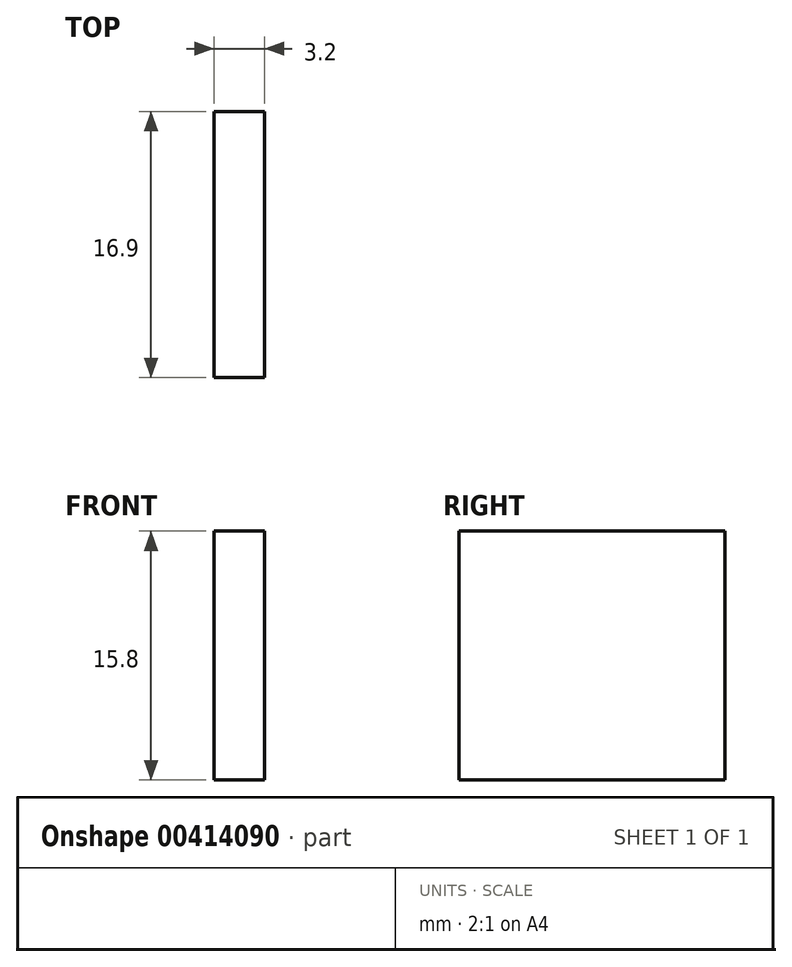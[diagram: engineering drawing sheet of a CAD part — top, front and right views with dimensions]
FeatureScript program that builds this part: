
annotation { "Feature Type Name" : "Feature", "Feature Type Description" : "" }
export const myFeature = defineFeature(function(context is Context, id is Id, definition is map)
    precondition{}
    {
        {
            var Q0;
            Q0=qCreatedBy(makeId("Front.planeOp"),FACE);
            var sketch = newSketch(context, id + "F0", { "sketchPlane" : qUnion([Q0])});
            skLineSegment(sketch, "E0.bottom", {"start": v(0, 0) * mm, "end": v(3.2, 0) * mm});
            skLineSegment(sketch, "E0.top", {"start": v(0, -15.8) * mm, "end": v(3.2, -15.8) * mm});
            skLineSegment(sketch, "E0.left", {"start": v(0, 0) * mm, "end": v(0, -15.8) * mm});
            skLineSegment(sketch, "E0.right", {"start": v(3.2, 0) * mm, "end": v(3.2, -15.8) * mm});
            skSolve(sketch);
        }
        {
            var Q0;
            Q0=makeQuery(id+"F0.imprint","IMPRINT",FACE,{"disambiguationData":[TD([[makeQuery(id+"F0.imprint","IMPRINT",EDGE,{"derivedFrom":sQuery(id+"F0.wireOp",EDGE,"E0.bottom")}),-1.0]])]});
            extrude(context, id + "F1", {"entities" : qUnion([Q0]), "depth" : 16.9 * mm});
        }
    });
